# Revit family: Shower_Slide_Bar-Grohe-26603_Series
name_source: partatom
category: Plumbing Fixtures
revit_build: Autodesk Revit 2018 (Build: 20170223_1515(x64)
units: mm (PartAtom-declared; Revit-internal decimal feet)

## family parameters
Cut with Voids When Loaded = No
Host = Face
OmniClass Number = 23.45.05.14.17
OmniClass Title = Showers
Part Type = Normal
Room Calculation Point = No
Round Connector Dimension = Use Diameter
Shared = Yes

## types (5) — shared parameters
ADA Compliant = Yes
Assembly Code = D2010710
CW Connection = Yes
Default Elevation = 0"
Description = 36inches Shower Slide Bar
HW Connection = Yes
Height = 43 13/16"
Installation Type = Wall Mounted
Length = 7 1/8"
Manufacturer = Grohe
Price = Prices may vary. Please consult Manufacturer Representative for most up-to-date price list.
Product Documentation Link = https://americanstandard.box.com
Product Page URL = https://www.grohe.us
Region = North America
URL = https://www.grohe.us
Vent Connection = No
Warranty Information = Limited Lifetime Warranty
Waste Connection = No
Width = 6 21/32"
zero-valued in all types: CWFU, HWFU, WFU

## per-type parameters (varying)
| type | Body Material | Material |
| 26603GN0 | Metal-Grohe-GN0-Brushed Cool Sunrise | Metal-Grohe-GN0-Brushed Cool Sunrise |
| 26603EN0 | Metal-Grohe-EN0-Brushed Nickel Infinity Finish | Metal-Grohe-EN0-Brushed Nickel Infinity Finish |
| 26603BE0 | Metal-Grohe-BE0-Polished Nickel Infinity Finish | Metal-Grohe-BE0-Polished Nickel Infinity Finish |
| 26603A00 | Metal-Grohe-A00-Hard Graphite | Metal-Grohe-A00-Hard Graphite |
| 26603000 | Metal-Grohe-000-Starlight Chrome | Metal-Grohe-000-Starlight Chrome |

note: column(s) folded — value = type name in every type: Model

## geometry (parser evidence)
native form markers: Sweep x3
no freeform markers — native parametric forms only
